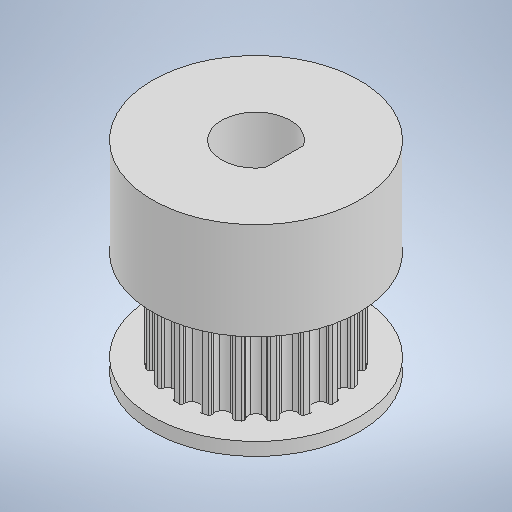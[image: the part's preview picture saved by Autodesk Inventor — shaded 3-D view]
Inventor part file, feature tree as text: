
AUTODESK INVENTOR PART (.ipt)
format: ipt  version: 2025.2 (Build 292293000, 293)  size: 569,856 bytes
history: native  units: mm
features: extrude x5, sketch x3, pattern_circular x1, mirror x1
ambient origin geometry x8: Origin, YZ Plane, XZ Plane, XY Plane, X Axis, Y Axis, Z Axis, Center Point
bodies: Solid1 (feature_tree)
feature tree (10):
  sketch  "Sketch1"  dims[d0=12.732395mm d1=1.570796mm]
  extrude  "Extrusion1"  Depth=1.570796mm
  extrude  "Extrusion2"  Depth=1.004mm
  extrude  "Extrusion3"  Depth=0.555mm
  pattern_circular  "Circular Pattern1"  [2 undecoded]
  mirror  "Mirror3"
  extrude  "Extrusion4"  Depth=0.15mm
  extrude  "Extrusion5"  Depth=4.5mm TaperAngle=0.0deg
  sketch  "Sketch2"  dims[d2=0.628319mm d4=1.004mm]
  sketch  "Sketch3"  dims[d13=0.75mm d14=0.555mm d15=1.0mm d16=0.15mm d18=4.5mm d19=0.0mm d20=3.5mm d21=0.0mm d22=3.5mm d23=0.0mm d24=200.0mm d25=360.0deg d27=5.3mm d28=0.0mm d29=0.0mm d31=2.2mm d33=7.5mm d34=0.0mm d35=16.0mm]
note: 2 required parameter values undecoded (feature->parameter linkage not recoverable at this tier; creation-order binding heuristic only, values carry confidence <= 0.55)
